# Revit family: Door_Lift_UltiGroup_FasTrax FR Wrapback
name_source: partatom
category: Doors
revit_build: Autodesk Revit 2018 (Build: 20170223_1515(x64)
units: mm (PartAtom-declared; Revit-internal decimal feet)

## family parameters
Always vertical = Yes
Cut with Voids When Loaded = No
Host = Wall
OmniClass Number = 23.30.10.21.17.11
OmniClass Title = Cold Storage Doors
Room Calculation Point = No
Shared = No

## types (1)
- 2HP - 3 Phase - 575V
    Analytic Construction = <None>
    Controls height from floor = 1400 mm  [stored 4.59318 ft]
    Description = High Speed Fabric Door for Cold Storage - FR Wrapback Lift
    DoorFrameFinish_ANZRS = Powder Coated Aluminium
    DoorFrameMaterial_ANZRS = Metal - Aluminum - Powder Coat - Black
    DoorFrameType_ANZRS = Aluminium Frame
    DoorGlazingHeight_ANZRS = 0 mm  [stored 0 ft]
    DoorGlazingWidth_ANZRS = 0 mm  [stored 0 ft]
    DoorGrilleHeight_ANZRS = 0 mm  [stored 0 ft]
    DoorGrilleWidth_ANZRS = 0 mm  [stored 0 ft]
    DoorGrille_ANZRS = No
    DoorNumberOfPanels_ANZRS = 0
    DoorOperation_ANZRS = [Induction Loop][Motion Sensor][Electronic Eye][Push Button Control][Radio Control][Pull Cord Manual Open]
    DoorPanelBWidth_ANZRS = 0 mm  [stored 0 ft]
    DoorPanelDepth_ANZRS = 0 mm  [stored 0 ft]
    DoorPanelFinish_ANZRS = PVC Fabric curtain with Insulation
    DoorPanelHeight_ANZRS = 4000 mm  [stored 13.1234 ft]
    DoorPanelMaterial_ANZRS = Fabric - Curtain - Blue
    DoorPanelWidth_ANZRS = 2944 mm  [stored 9.65879 ft]
    Expected Lifespan (Years) = 0
    Fax = 07 846 2467
    Function = Interior
    Height = 4000 mm  [stored 13.1234 ft]
    Height of Wrapback = 2400 mm
    Installation Phase = Exterior Enclosure
    InstallationGroup_ANZRS = 0
    LH = Yes
    Maintenance Schedule (Months) = 0
    Manufacturer = UltiGroup
    Max Height = 4877 mm
    Max Width = 2500 mm
    Min Height = 2134 mm
    Min Width = 1524 mm  [stored 5 ft]
    Model = Ulti FasTrax FR - Wrapback Lift
    ModifiedIssue_ANZRS = 0 $
    Motor HP = 2
    Phase = 3
    Power Isolator distance = 1200 mm
    RH = No
    RO Spacing = 222 mm
    Rough Height = 3778 mm
    Rough Width = 2500 mm
    Send Message = http://ultigroup.co.nz
    Supply to ceiling = 200 mm  [stored 0.656168 ft]
    Thickness = 25 mm  [stored 0.082021 ft]
    URL = www.ultigroup.co.nz
    Voltage = 575
    Wall Closure = By host
    Warranty Duration (Years) = 0
    Width = 2944 mm  [stored 9.65879 ft]

note: [stored X ft] marks values corroborated as IEEE doubles in the binary element streams (Revit-internal decimal feet)

## geometry (parser evidence)
native form markers: Blend x6, Sweep x2
no freeform markers — native parametric forms only
